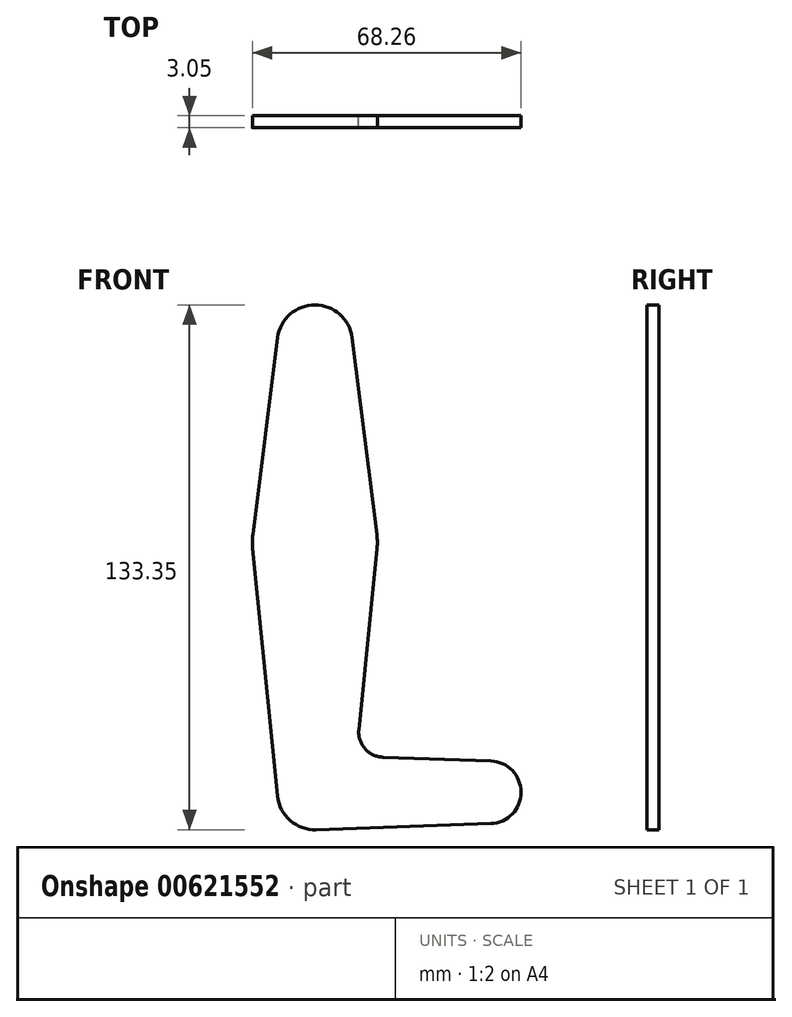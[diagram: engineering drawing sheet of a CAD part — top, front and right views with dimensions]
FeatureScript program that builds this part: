
annotation { "Feature Type Name" : "Feature", "Feature Type Description" : "" }
export const myFeature = defineFeature(function(context is Context, id is Id, definition is map)
    precondition{}
    {
        {
            var Q0;
            Q0=qCreatedBy(makeId("Front.planeOp"),FACE);
            var sketch = newSketch(context, id + "F0", { "sketchPlane" : qUnion([Q0])});
            skLineSegment(sketch, "E0", {"start": v(44.45, 0) * mm, "end": v(0, 0) * mm, "construction": true});
            skLineSegment(sketch, "E1", {"start": v(0, 0) * mm, "end": v(0, 114.3) * mm, "construction": true});
            skCircle(sketch, "E2", {"center": v(44.45, 0) * mm, "radius": 7.94 * mm});
            skCircle(sketch, "E3", {"center": v(0, 0) * mm, "radius": 9.53 * mm});
            skCircle(sketch, "E4", {"center": v(0, 63.5) * mm, "radius": 15.88 * mm});
            skCircle(sketch, "E5", {"center": v(0, 114.3) * mm, "radius": 9.53 * mm});
            skLineSegment(sketch, "E6", {"start": v(-9.45, 115.5) * mm, "end": v(-15.75, 65.48) * mm});
            skLineSegment(sketch, "E7", {"start": v(-15.8, 61.91) * mm, "end": v(-9.48, -0.95) * mm});
            skLineSegment(sketch, "E8", {"start": v(15.8, 61.91) * mm, "end": v(11.17, 15.9) * mm});
            skLineSegment(sketch, "E9", {"start": v(9.45, 115.5) * mm, "end": v(15.75, 65.48) * mm});
            skLineSegment(sketch, "E10", {"start": v(44.73, 7.93) * mm, "end": v(17.26, 8.91) * mm});
            skLineSegment(sketch, "E11", {"start": v(44.73, -7.93) * mm, "end": v(0.34, -9.52) * mm});
            skArc(sketch, "E12.filletArc", {"start": v(11.17, 15.9) * mm, "mid": v(12.7, 11.09) * mm, "end": v(17.26, 8.91) * mm});
            skSolve(sketch);
        }
        {
            var Q0;
            {var subQ0=sQuery(id+"F0.wireOp",EDGE,"E6");Q0=makeQuery(id+"F0.imprint","IMPRINT",FACE,{"disambiguationData":[TD([[makeQuery(id+"F0.imprint","IMPRINT",EDGE,{"derivedFrom":subQ0}),1.0]])]});}
            var Q1;
            {var subQ0=sQuery(id+"F0.wireOp",EDGE,"E5");var subQ1=makeQuery(id+"F0.imprint","INTERSECT",VERTEX,{"derivedFrom":[subQ0,sQuery(id+"F0.wireOp",EDGE,"E6")]});Q1=makeQuery(id+"F0.imprint","IMPRINT",FACE,{"disambiguationData":[TD([[makeQuery(id+"F0.imprint","IMPRINT",EDGE,{"disambiguationData":[TD([[subQ1,1.0]])],"derivedFrom":subQ0}),1.0]])]});}
            var Q2;
            {var subQ0=sQuery(id+"F0.wireOp",EDGE,"E4");var subQ1=makeQuery(id+"F0.imprint","INTERSECT",VERTEX,{"derivedFrom":[subQ0,sQuery(id+"F0.wireOp",EDGE,"E6")]});Q2=makeQuery(id+"F0.imprint","IMPRINT",FACE,{"disambiguationData":[TD([[makeQuery(id+"F0.imprint","IMPRINT",EDGE,{"disambiguationData":[TD([[subQ1,1.0]])],"derivedFrom":subQ0}),1.0]])]});}
            var Q3;
            {var subQ0=sQuery(id+"F0.wireOp",EDGE,"E7");Q3=makeQuery(id+"F0.imprint","IMPRINT",FACE,{"disambiguationData":[TD([[makeQuery(id+"F0.imprint","IMPRINT",EDGE,{"derivedFrom":subQ0}),1.0]])]});}
            var Q4;
            {var subQ0=sQuery(id+"F0.wireOp",EDGE,"E3");var subQ1=makeQuery(id+"F0.imprint","INTERSECT",VERTEX,{"derivedFrom":[subQ0,sQuery(id+"F0.wireOp",EDGE,"E7")]});Q4=makeQuery(id+"F0.imprint","IMPRINT",FACE,{"disambiguationData":[TD([[makeQuery(id+"F0.imprint","IMPRINT",EDGE,{"disambiguationData":[TD([[subQ1,-1.0]])],"derivedFrom":subQ0}),1.0]])]});}
            var Q5;
            {var subQ0=sQuery(id+"F0.wireOp",EDGE,"E2");var subQ1=makeQuery(id+"F0.imprint","INTERSECT",VERTEX,{"derivedFrom":[subQ0,sQuery(id+"F0.wireOp",EDGE,"E10")]});Q5=makeQuery(id+"F0.imprint","IMPRINT",FACE,{"disambiguationData":[TD([[makeQuery(id+"F0.imprint","IMPRINT",EDGE,{"disambiguationData":[TD([[subQ1,-1.0]])],"derivedFrom":subQ0}),1.0]])]});}
            extrude(context, id + "F1", {"entities" : qUnion([Q0, Q1, Q2, Q3, Q4, Q5]), "depth" : 3.05 * mm, "offsetDistance" : 25.4 * mm});
        }
    });
